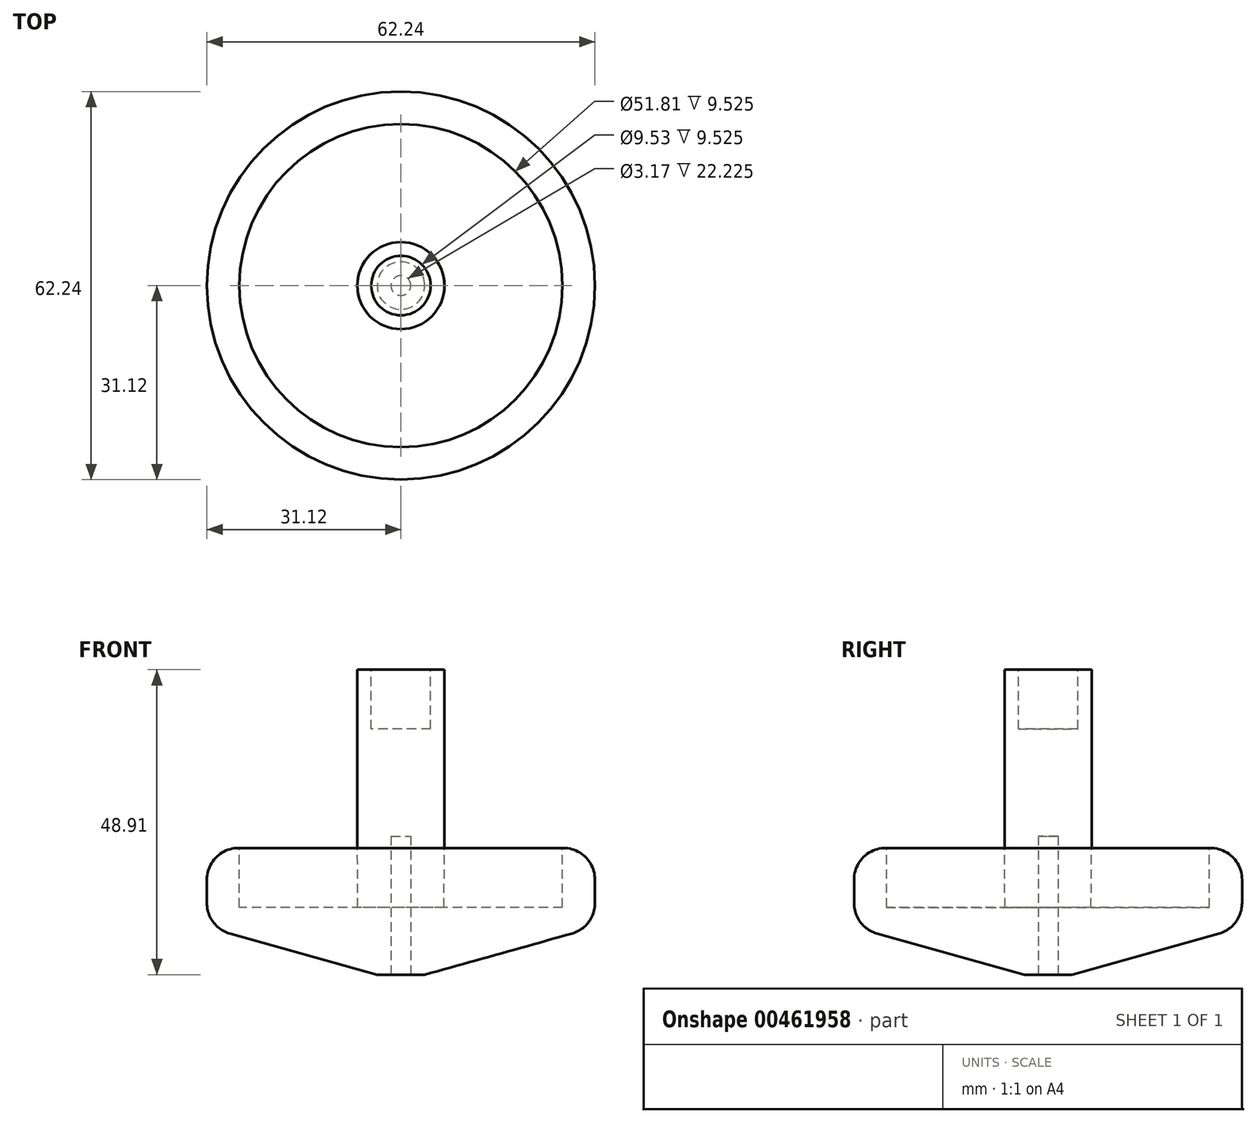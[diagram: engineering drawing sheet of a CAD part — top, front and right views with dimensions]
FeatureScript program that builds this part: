
annotation { "Feature Type Name" : "Feature", "Feature Type Description" : "" }
export const myFeature = defineFeature(function(context is Context, id is Id, definition is map)
    precondition{}
    {
        {
            var Q0;
            Q0=qCreatedBy(makeId("Front.planeOp"),FACE);
            var sketch = newSketch(context, id + "F0", { "sketchPlane" : qUnion([Q0])});
            skLineSegment(sketch, "E0", {"start": v(31.12, 9.5) * mm, "end": v(31.12, 22.2) * mm});
            skLineSegment(sketch, "E1", {"start": v(6.99, 50.8) * mm, "end": v(0, 50.8) * mm});
            skLineSegment(sketch, "E2", {"start": v(0, 50.8) * mm, "end": v(0, 1.89) * mm});
            skLineSegment(sketch, "E3", {"start": v(0, 1.89) * mm, "end": v(3.81, 1.89) * mm});
            skLineSegment(sketch, "E4", {"start": v(3.81, 1.89) * mm, "end": v(31.12, 9.5) * mm});
            skLineSegment(sketch, "E5", {"start": v(6.99, 22.2) * mm, "end": v(6.99, 50.8) * mm});
            skLineSegment(sketch, "E6", {"start": v(25.9, 22.2) * mm, "end": v(25.9, 12.68) * mm});
            skLineSegment(sketch, "E7", {"start": v(25.9, 12.68) * mm, "end": v(6.9, 12.68) * mm});
            skLineSegment(sketch, "E8", {"start": v(6.9, 12.68) * mm, "end": v(6.99, 22.2) * mm});
            skLineSegment(sketch, "E9", {"start": v(25.9, 22.2) * mm, "end": v(31.12, 22.2) * mm});
            skSolve(sketch);
        }
        {
            var Q0;
            Q0=makeQuery(id+"F0.imprint","IMPRINT",FACE,{"disambiguationData":[TD([[makeQuery(id+"F0.imprint","IMPRINT",EDGE,{"derivedFrom":sQuery(id+"F0.wireOp",EDGE,"E0")}),1.0]])]});
            var Q1;
            Q1=sQuery(id+"F0.wireOp",EDGE,"E2");
            revolve(context, id + "F1", {"entities" : qUnion([Q0]), "axis" : qUnion([Q1]), "revolveType" : RevolveType.FULL});
        }
        {
            var Q0;
            Q0=makeQuery(id+"F1.opRevolve","SWEPT_FACE",FACE,{"disambiguationData":[OSD([sQuery(id+"F0.wireOp",EDGE,"E1")])]});
            var sketch = newSketch(context, id + "F2", { "sketchPlane" : qUnion([Q0])});
            skCircle(sketch, "E10", {"center": v(0, 0) * mm, "radius": 4.76 * mm});
            skSolve(sketch);
        }
        {
            var Q0;
            Q0=makeQuery(id+"F2.imprint","IMPRINT",FACE,{"disambiguationData":[TD([[makeQuery(id+"F2.imprint","IMPRINT",EDGE,{"derivedFrom":sQuery(id+"F2.wireOp",EDGE,"E10")}),1.0]])]});
            extrude(context, id + "F3", {"entities" : qUnion([Q0]), "operationType" : NewBodyOperationType.REMOVE, "oppositeDirection" : true, "depth" : 9.52 * mm});
        }
        {
            var Q0;
            Q0=makeQuery(id+"F1.opRevolve","SWEPT_FACE",FACE,{"disambiguationData":[OSD([sQuery(id+"F0.wireOp",EDGE,"E3")])]});
            var sketch = newSketch(context, id + "F4", { "sketchPlane" : qUnion([Q0])});
            skCircle(sketch, "E11", {"center": v(0, 0) * mm, "radius": 1.59 * mm});
            skSolve(sketch);
        }
        {
            var Q0;
            Q0=qSketchRegion(id+"F4",true);
            extrude(context, id + "F5", {"entities" : qUnion([Q0]), "operationType" : NewBodyOperationType.REMOVE, "oppositeDirection" : true, "depth" : 22.22 * mm});
        }
        {
            var Q0;
            Q0=makeQuery(id+"F1.opRevolve","SWEPT_FACE",FACE,{"disambiguationData":[OSD([sQuery(id+"F0.wireOp",EDGE,"E0")])]});
            fillet(context, id + "F6", {"entities" : qUnion([Q0]), "radius" : 5.08 * mm, "tangentPropagation" : true, "allowEdgeOverflow" : false});
        }
    });
